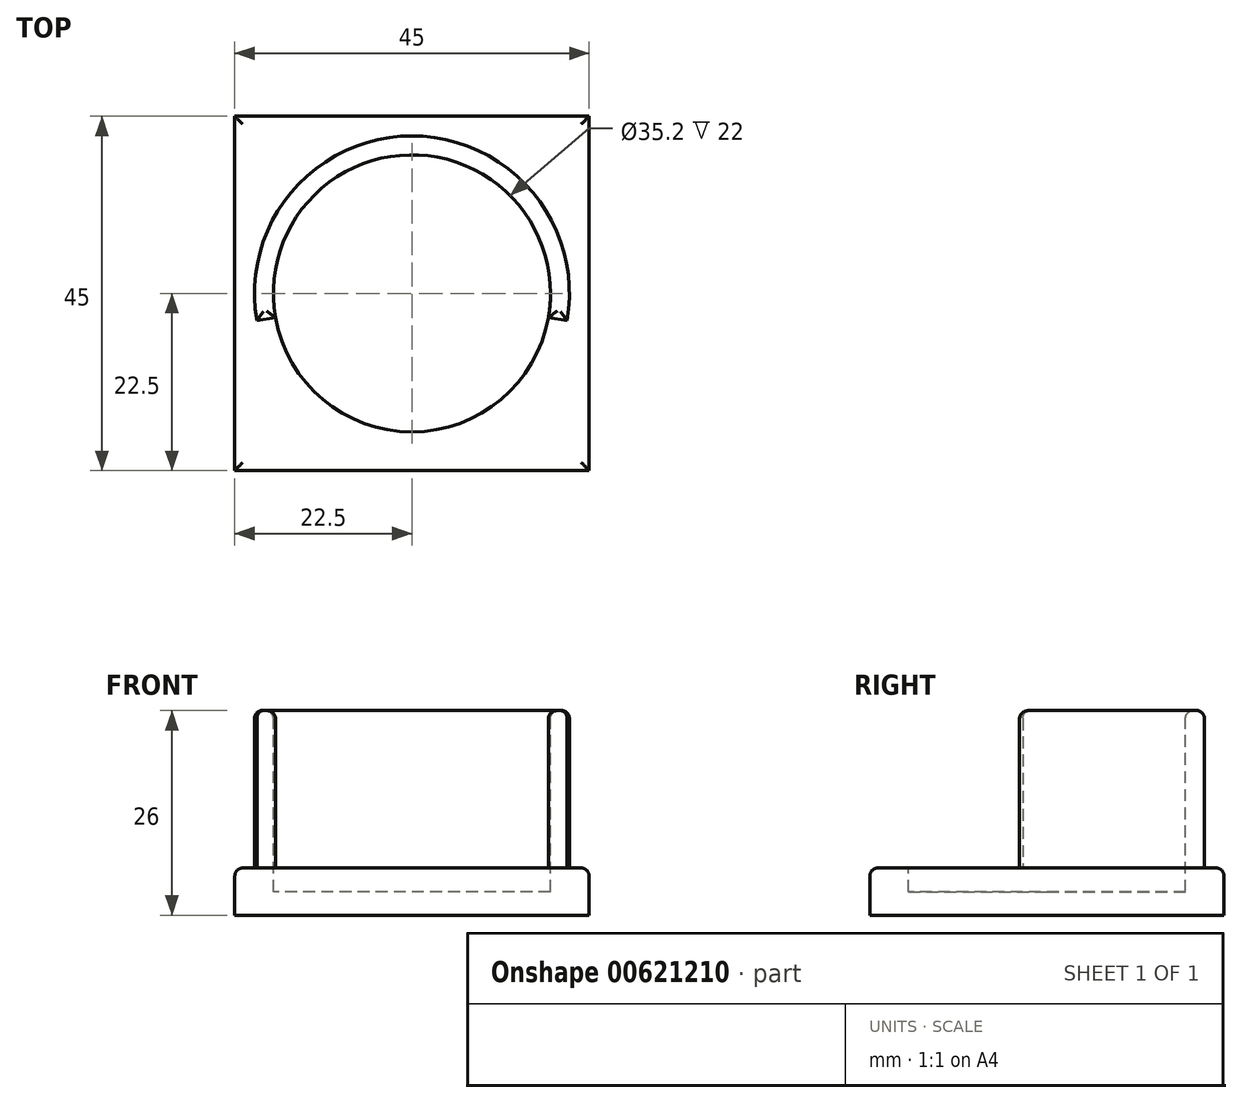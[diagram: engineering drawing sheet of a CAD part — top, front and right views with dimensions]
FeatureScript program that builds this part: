
annotation { "Feature Type Name" : "Feature", "Feature Type Description" : "" }
export const myFeature = defineFeature(function(context is Context, id is Id, definition is map)
    precondition{}
    {
        {
            var Q0;
            Q0=qCreatedBy(makeId("Top.planeOp"),FACE);
            var sketch = newSketch(context, id + "F0", { "sketchPlane" : qUnion([Q0])});
            skLineSegment(sketch, "E0.bottom", {"start": v(22.5, 22.5) * mm, "end": v(-22.5, 22.5) * mm});
            skLineSegment(sketch, "E0.top", {"start": v(22.5, -22.5) * mm, "end": v(-22.5, -22.5) * mm});
            skLineSegment(sketch, "E0.left", {"start": v(22.5, 22.5) * mm, "end": v(22.5, -22.5) * mm});
            skLineSegment(sketch, "E0.right", {"start": v(-22.5, 22.5) * mm, "end": v(-22.5, -22.5) * mm});
            skPoint(sketch, "E0.middle", {"position": v(0, 0) * mm});
            skSolve(sketch);
        }
        {
            var Q0;
            Q0=makeQuery(id+"F0.imprint","IMPRINT",FACE,{"disambiguationData":[TD([[makeQuery(id+"F0.imprint","IMPRINT",EDGE,{"derivedFrom":sQuery(id+"F0.wireOp",EDGE,"E0.bottom")}),1.0]])]});
            extrude(context, id + "F1", {"entities" : qUnion([Q0]), "depth" : 6 * mm, "offsetDistance" : 25 * mm});
        }
        {
            var Q0;
            Q0=makeQuery(id+"F1.opExtrude","CAP_FACE",FACE,{"disambiguationData":[OSD([sQuery(id+"F0.wireOp",EDGE,"E0.bottom"),sQuery(id+"F0.wireOp",EDGE,"E0.top"),sQuery(id+"F0.wireOp",EDGE,"E0.left"),sQuery(id+"F0.wireOp",EDGE,"E0.right")])],"isStart":false});
            var sketch = newSketch(context, id + "F2", { "sketchPlane" : qUnion([Q0])});
            skCircle(sketch, "E1", {"center": v(0, 0) * mm, "radius": 17.6 * mm});
            skSolve(sketch);
        }
        {
            var Q0;
            Q0=makeQuery(id+"F2.imprint","IMPRINT",FACE,{"disambiguationData":[TD([[makeQuery(id+"F2.imprint","IMPRINT",EDGE,{"derivedFrom":sQuery(id+"F2.wireOp",EDGE,"E1")}),1.0]])]});
            extrude(context, id + "F3", {"entities" : qUnion([Q0]), "operationType" : NewBodyOperationType.REMOVE, "oppositeDirection" : true, "depth" : 3 * mm, "offsetDistance" : 25 * mm});
        }
        {
            var Q0;
            Q0=makeQuery(id+"F1.opExtrude","CAP_FACE",FACE,{"disambiguationData":[OSD([sQuery(id+"F0.wireOp",EDGE,"E0.bottom"),sQuery(id+"F0.wireOp",EDGE,"E0.top"),sQuery(id+"F0.wireOp",EDGE,"E0.left"),sQuery(id+"F0.wireOp",EDGE,"E0.right")])],"isStart":false});
            var sketch = newSketch(context, id + "F4", { "sketchPlane" : qUnion([Q0])});
            skCircle(sketch, "E2", {"center": v(0, 0) * mm, "radius": 20 * mm});
            skCircle(sketch, "E3", {"center": v(0, 0) * mm, "radius": 17.6 * mm});
            skLineSegment(sketch, "E4", {"start": v(0, 0) * mm, "end": v(-19.7, -3.47) * mm});
            skLineSegment(sketch, "E5", {"start": v(0, 0) * mm, "end": v(19.7, -3.47) * mm});
            skSolve(sketch);
        }
        {
            var Q0;
            {var subQ0=sQuery(id+"F4.wireOp",EDGE,"E4");var subQ1=sQuery(id+"F4.wireOp",EDGE,"E2");var subQ2=makeQuery(id+"F4.imprint","INTERSECT",VERTEX,{"derivedFrom":[subQ1,subQ0]});Q0=makeQuery(id+"F4.imprint","IMPRINT",FACE,{"disambiguationData":[TD([[makeQuery(id+"F4.imprint","IMPRINT",EDGE,{"disambiguationData":[TD([[subQ2,1.0]])],"derivedFrom":subQ1}),1.0]])]});}
            extrude(context, id + "F5", {"entities" : qUnion([Q0]), "operationType" : NewBodyOperationType.ADD, "depth" : 20 * mm, "offsetDistance" : 25 * mm});
        }
        {
            var Q0;
            Q0=makeQuery(id+"F1.opExtrude","CAP_EDGE",EDGE,{"disambiguationData":[OSD([sQuery(id+"F0.wireOp",EDGE,"E0.top")])],"isStart":false});
            var Q1;
            Q1=makeQuery(id+"F1.opExtrude","CAP_EDGE",EDGE,{"disambiguationData":[OSD([sQuery(id+"F0.wireOp",EDGE,"E0.left")])],"isStart":false});
            var Q2;
            Q2=makeQuery(id+"F1.opExtrude","CAP_EDGE",EDGE,{"disambiguationData":[OSD([sQuery(id+"F0.wireOp",EDGE,"E0.bottom")])],"isStart":false});
            var Q3;
            Q3=makeQuery(id+"F1.opExtrude","CAP_EDGE",EDGE,{"disambiguationData":[OSD([sQuery(id+"F0.wireOp",EDGE,"E0.right")])],"isStart":false});
            var Q4;
            Q4=makeQuery(id+"F5.opExtrude","CAP_EDGE",EDGE,{"disambiguationData":[OSD([sQuery(id+"F4.wireOp",EDGE,"E3")])],"isStart":false});
            var Q5;
            Q5=makeQuery(id+"F5.opExtrude","CAP_EDGE",EDGE,{"disambiguationData":[OSD([sQuery(id+"F4.wireOp",EDGE,"E2")])],"isStart":false});
            var Q6;
            Q6=makeQuery(id+"F5.opExtrude","CAP_EDGE",EDGE,{"disambiguationData":[OSD([sQuery(id+"F4.wireOp",EDGE,"E4")])],"isStart":false});
            var Q7;
            Q7=makeQuery(id+"F5.opExtrude","CAP_EDGE",EDGE,{"disambiguationData":[OSD([sQuery(id+"F4.wireOp",EDGE,"E5")])],"isStart":false});
            fillet(context, id + "F6", {"entities" : qUnion([Q0, Q1, Q2, Q3, Q4, Q5, Q6, Q7]), "radius" : 1 * mm, "tangentPropagation" : true, "allowEdgeOverflow" : false});
        }
    });
